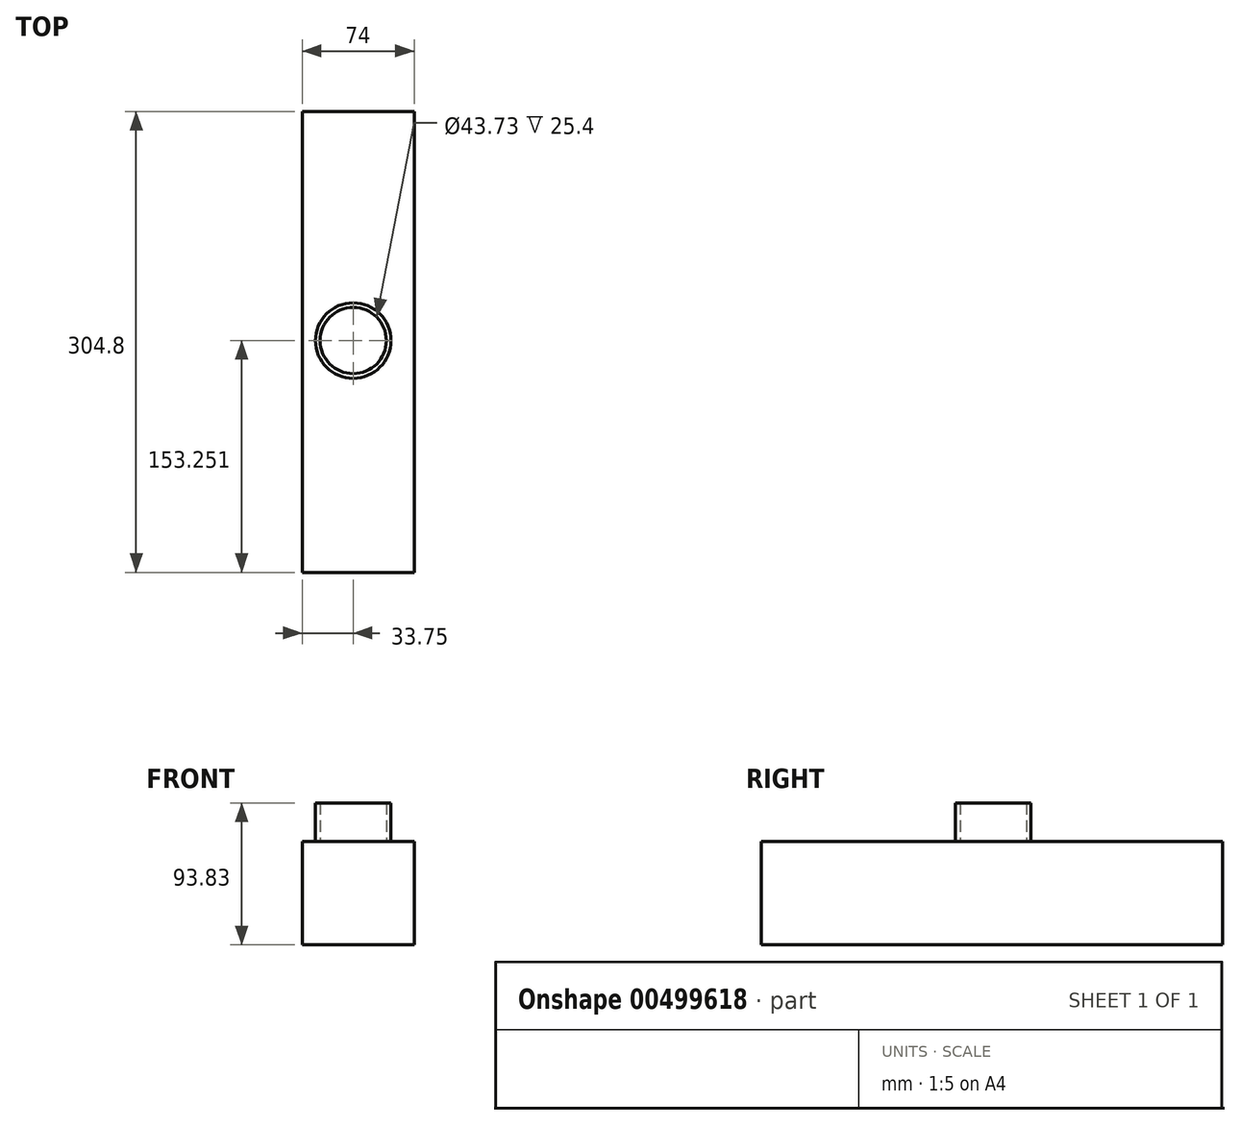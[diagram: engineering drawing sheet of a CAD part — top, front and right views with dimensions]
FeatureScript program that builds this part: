
annotation { "Feature Type Name" : "Feature", "Feature Type Description" : "" }
export const myFeature = defineFeature(function(context is Context, id is Id, definition is map)
    precondition{}
    {
        {
            var Q0;
            Q0=qCreatedBy(makeId("Front.planeOp"),FACE);
            var sketch = newSketch(context, id + "F0", { "sketchPlane" : qUnion([Q0])});
            skLineSegment(sketch, "E0.bottom", {"start": v(-33.75, 41.18) * mm, "end": v(40.25, 41.18) * mm});
            skLineSegment(sketch, "E0.top", {"start": v(-33.75, -27.25) * mm, "end": v(40.25, -27.25) * mm});
            skLineSegment(sketch, "E0.left", {"start": v(-33.75, 41.18) * mm, "end": v(-33.75, -27.25) * mm});
            skLineSegment(sketch, "E0.right", {"start": v(40.25, 41.18) * mm, "end": v(40.25, -27.25) * mm});
            skSolve(sketch);
        }
        {
            var Q0;
            Q0=makeQuery(id+"F0.imprint","IMPRINT",FACE,{"disambiguationData":[TD([[makeQuery(id+"F0.imprint","IMPRINT",EDGE,{"derivedFrom":sQuery(id+"F0.wireOp",EDGE,"E0.bottom")}),-1.0]])]});
            extrude(context, id + "F1", {"entities" : qUnion([Q0]), "depth" : 304.8 * mm});
        }
        {
            var Q0;
            Q0=makeQuery(id+"F1.opExtrude","SWEPT_FACE",FACE,{"disambiguationData":[OSD([sQuery(id+"F0.wireOp",EDGE,"E0.bottom")])]});
            var sketch = newSketch(context, id + "F2", { "sketchPlane" : qUnion([Q0])});
            skCircle(sketch, "E1", {"center": v(0, -151.55) * mm, "radius": 24.96 * mm});
            skCircle(sketch, "E2", {"center": v(0, -151.55) * mm, "radius": 21.87 * mm});
            skCircle(sketch, "E3", {"center": v(0, -151.55) * mm, "radius": 15.78 * mm});
            skSolve(sketch);
        }
        {
            var Q0;
            Q0 = qSketchRegion(id + "F2", true);
            extrude(context, id + "F3", {"entities" : qUnion([Q0]), "operationType" : NewBodyOperationType.ADD, "depth" : 25.4 * mm});
        }
    });
